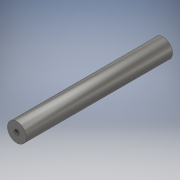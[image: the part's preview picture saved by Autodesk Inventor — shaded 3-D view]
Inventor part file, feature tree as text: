
AUTODESK INVENTOR PART (.ipt)
format: ipt  version: 2019 (Build 230136000, 136)  size: 107,008 bytes
history: native  units: in
note: dims shown in document units (in); Inventor stores cm internally (conversion verified against a paired STEP export)
features: sketch x3, hole x2, extrude x1
ambient origin geometry x8: Origin, YZ Plane, XZ Plane, XY Plane, X Axis, Y Axis, Z Axis, Center Point
bodies: Solid1 (feature_tree)
feature tree (6):
  extrude  "Extrusion1"  Depth=5.827in TaperAngle=0.0deg
  sketch  "Sketch2"  dims[d3=0.196in d4=0.5in d5=0.507in d6=0.25in d7=0.5635in d8=0.75in d9=0.8108in]
  hole  "Hole1"  [1 undecoded]
  hole  "Hole2"  [1 undecoded]
  sketch  "Sketch1"  dims[d0=0.75in d1=5.827in d2=0.0in]
  sketch  "Sketch3"  dims[d10=0.196in d11=0.5in d12=0.507in d13=0.25in d14=0.5635in d15=0.75in d16=0.8108in]
note: 2 required parameter values undecoded (feature->parameter linkage not recoverable at this tier; creation-order binding heuristic only, values carry confidence <= 0.55)
